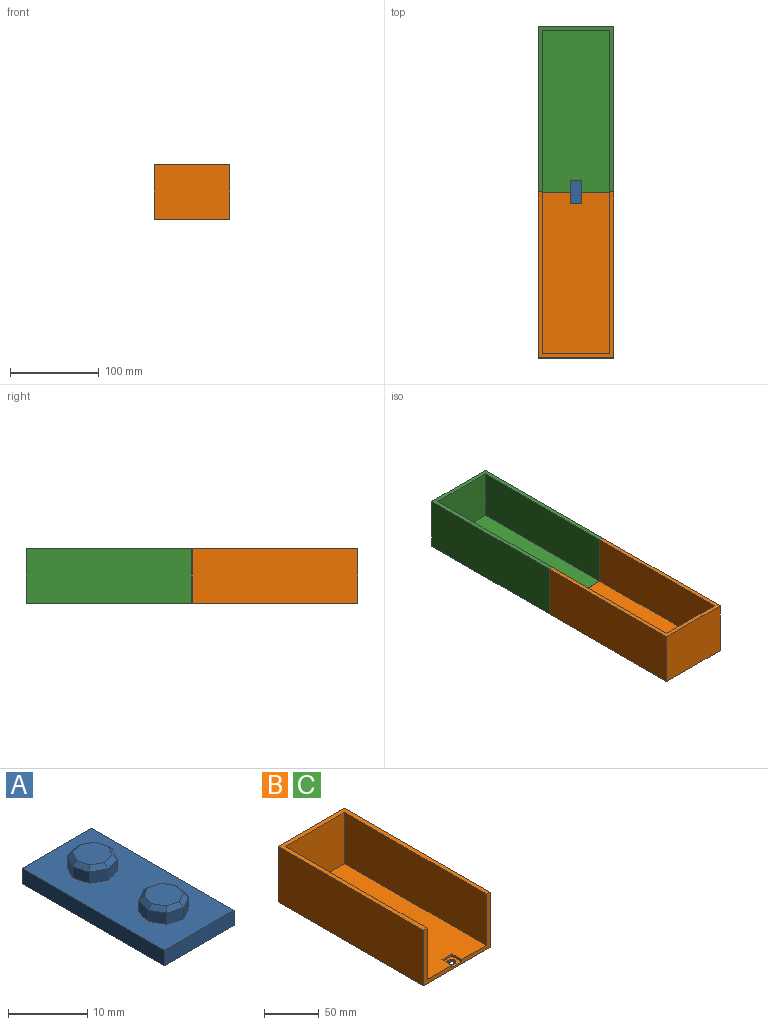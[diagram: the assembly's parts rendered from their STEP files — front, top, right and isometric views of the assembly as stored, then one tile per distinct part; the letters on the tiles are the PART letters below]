
ASSEMBLY  parts=3 mates=5
PART A: 40 faces, bbox 12.4x25.4x4.7 mm
  f0: plane 25.4x12.45mm, normal (0,0,1), area 259.1mm2, adj f1,f2,f3,f5,f6,f7,f8,f9
  f1: plane 25.4x2.36mm, normal (1,0,0), area 60mm2, adj f0,f3,f4,f14
  f2: plane 25.4x2.36mm, normal (-1,0,0), area 60mm2, adj f0,f3,f4,f14
  f3: plane 12.45x2.36mm, normal (0,-1,0), area 29.4mm2, adj f0,f1,f2,f4
  f4: plane 25.4x12.45mm, normal (0,0,-1), area 316.1mm2, adj f1,f2,f3,f14
  f5: plane 2.35x1.73mm, normal (0.26,0.97,0), area 4.2mm2, adj f0,f6,f12,f38
  f6: plane 2.1x1.73mm, normal (-0.5,0.87,0), area 4.2mm2, adj f0,f5,f7,f39
  f7: plane 2.35x1.73mm, normal (-0.97,0.26,0), area 4.2mm2, adj f0,f6,f8,f37
  f8: plane 2.1x1.73mm, normal (-0.87,-0.5,0), area 4.2mm2, adj f0,f7,f9,f35
  f9: plane 2.35x1.73mm, normal (-0.26,-0.97,0), area 4.2mm2, adj f0,f8,f10,f33
  f10: plane 2.1x1.73mm, normal (0.5,-0.87,0), area 4.2mm2, adj f0,f9,f11,f32
  f11: plane 2.35x1.73mm, normal (0.97,-0.26,0), area 4.2mm2, adj f0,f10,f12,f34
  f12: plane 2.1x1.73mm, normal (0.87,0.5,0), area 4.2mm2, adj f0,f5,f11,f36
  f13: plane 4.93x4.93mm, normal (0,0,1), area 17.5mm2, adj f32,f33,f34,f35,f36,f37,f38,f39
  f14: plane 12.45x2.36mm, normal (0,1,0), area 29.4mm2, adj f0,f1,f2,f4
  f15: plane 2.35x1.73mm, normal (0.26,-0.97,0), area 4.2mm2, adj f0,f16,f22,f30
  f16: plane 2.1x1.73mm, normal (-0.5,-0.87,0), area 4.2mm2, adj f0,f15,f17,f31
  f17: plane 2.35x1.73mm, normal (-0.97,-0.26,0), area 4.2mm2, adj f0,f16,f18,f29
  f18: plane 2.1x1.73mm, normal (-0.87,0.5,0), area 4.2mm2, adj f0,f17,f19,f27
  f19: plane 2.35x1.73mm, normal (-0.26,0.97,0), area 4.2mm2, adj f0,f18,f20,f25
  f20: plane 2.1x1.73mm, normal (0.5,0.87,0), area 4.2mm2, adj f0,f19,f21,f24
  f21: plane 2.35x1.73mm, normal (0.97,0.26,0), area 4.2mm2, adj f0,f20,f22,f26
  f22: plane 2.1x1.73mm, normal (0.87,-0.5,0), area 4.2mm2, adj f0,f15,f21,f28
  f23: plane 4.93x4.93mm, normal (0,0,1), area 17.5mm2, adj f24,f25,f26,f27,f28,f29,f30,f31
  f24: plane 2.19x1.64mm, normal (0.35,0.61,0.71), area 1.9mm2, adj f20,f23,f25,f26
  f25: plane 2.35x1.17mm, normal (-0.18,0.68,0.71), area 1.9mm2, adj f19,f23,f24,f27
  f26: plane 2.35x1.17mm, normal (0.68,0.18,0.71), area 1.9mm2, adj f21,f23,f24,f28
  f27: plane 2.19x1.64mm, normal (-0.61,0.35,0.71), area 1.9mm2, adj f18,f23,f25,f29
  f28: plane 2.19x1.64mm, normal (0.61,-0.35,0.71), area 1.9mm2, adj f22,f23,f26,f30
  f29: plane 2.35x1.17mm, normal (-0.68,-0.18,0.71), area 1.9mm2, adj f17,f23,f27,f31
  f30: plane 2.35x1.17mm, normal (0.18,-0.68,0.71), area 1.9mm2, adj f15,f23,f28,f31
  f31: plane 2.19x1.64mm, normal (-0.35,-0.61,0.71), area 1.9mm2, adj f16,f23,f29,f30
  f32: plane 2.19x1.64mm, normal (0.35,-0.61,0.71), area 1.9mm2, adj f10,f13,f33,f34
  f33: plane 2.35x1.17mm, normal (-0.18,-0.68,0.71), area 1.9mm2, adj f9,f13,f32,f35
  f34: plane 2.35x1.17mm, normal (0.68,-0.18,0.71), area 1.9mm2, adj f11,f13,f32,f36
  f35: plane 2.19x1.64mm, normal (-0.61,-0.35,0.71), area 1.9mm2, adj f8,f13,f33,f37
  f36: plane 2.19x1.64mm, normal (0.61,0.35,0.71), area 1.9mm2, adj f12,f13,f34,f38
  f37: plane 2.35x1.17mm, normal (-0.68,0.18,0.71), area 1.9mm2, adj f7,f13,f35,f39
  f38: plane 2.35x1.17mm, normal (0.18,0.68,0.71), area 1.9mm2, adj f5,f13,f36,f39
  f39: plane 2.19x1.64mm, normal (-0.35,0.61,0.71), area 1.9mm2, adj f6,f13,f37,f38
PART B: 16 faces, bbox 85.7x187.3x61.9 mm
  f0: plane 182.56x76.2mm, normal (0,0,1), area 13750.3mm2, adj f1,f6,f7,f9,f10,f11,f12
  f1: plane 85.73x61.91mm, normal (0,-1,0), area 922.4mm2, adj f0,f2,f3,f4,f5,f6,f7,f10
  f2: plane 187.33x85.73mm, normal (0,0,1), area 2147.2mm2, adj f1,f3,f4,f6,f7,f8,f9
  f3: plane 187.33x61.91mm, normal (1,0,0), area 11597.8mm2, adj f1,f2,f5,f8
  f4: plane 187.33x61.91mm, normal (-1,0,0), area 11597.8mm2, adj f1,f2,f5,f8
  f5: plane 187.33x85.73mm, normal (0,0,-1), area 16026.8mm2, adj f1,f3,f4,f8,f14
  f6: plane 182.56x57.15mm, normal (-1,0,0), area 10433.4mm2, adj f0,f1,f2,f9
  f7: plane 182.56x57.15mm, normal (1,0,0), area 10433.4mm2, adj f0,f1,f2,f9
  f8: plane 85.73x61.91mm, normal (0,1,0), area 5307.4mm2, adj f2,f3,f4,f5
  f9: plane 76.2x57.15mm, normal (0,-1,0), area 4354.8mm2, adj f0,f2,f6,f7
  f10: plane 12.67x2.38mm, normal (1,0,0), area 30.2mm2, adj f0,f1,f12,f13
  f11: plane 12.67x2.38mm, normal (-1,0,0), area 30.2mm2, adj f0,f1,f12,f13
  f12: plane 12.7x2.38mm, normal (0,-1,0), area 30.2mm2, adj f0,f10,f11,f13
  f13: plane 12.7x12.67mm, normal (0,0,1), area 115.4mm2, adj f1,f10,f11,f12,f15
  f14: cylinder r=3.17mm len=6.35mm, axis (0,0,1), area 34.8mm2, adj f5,f15
  f15: cone r=3.17mm half-angle=45deg, axis (0,0,1), area 19.7mm2, adj f13,f14
PART C: same geometry as B
PLACE A rot(axis=(0,1,0),180deg) t=(9.48,-217.77,-43.14)mm
PLACE B rot(axis=(0,0,-1),180deg) t=(9.48,-217.78,-47.88)mm
PLACE C t=(9.48,-217.76,-47.88)mm
MATE slider B.f14 <-> A.f13  axis (0,0,1) through (9.48,-224.12,-46.13)mm
MATE planar C.f14 <-> A.f0  axis (0,0,1) through (9.48,-211.42,-45.5)mm
MATE slider A.f23 <-> C.f14  axis (0,0,-1) through (9.48,-211.42,-47.86)mm
MATE planar A.f0 <-> B.f14  axis (0,0,-1) through (9.48,-217.77,-45.5)mm
MATE parallel B.f1 <-> C.f1  axis (0,1,0) through (-33.38,-217.78,14.03)mm
